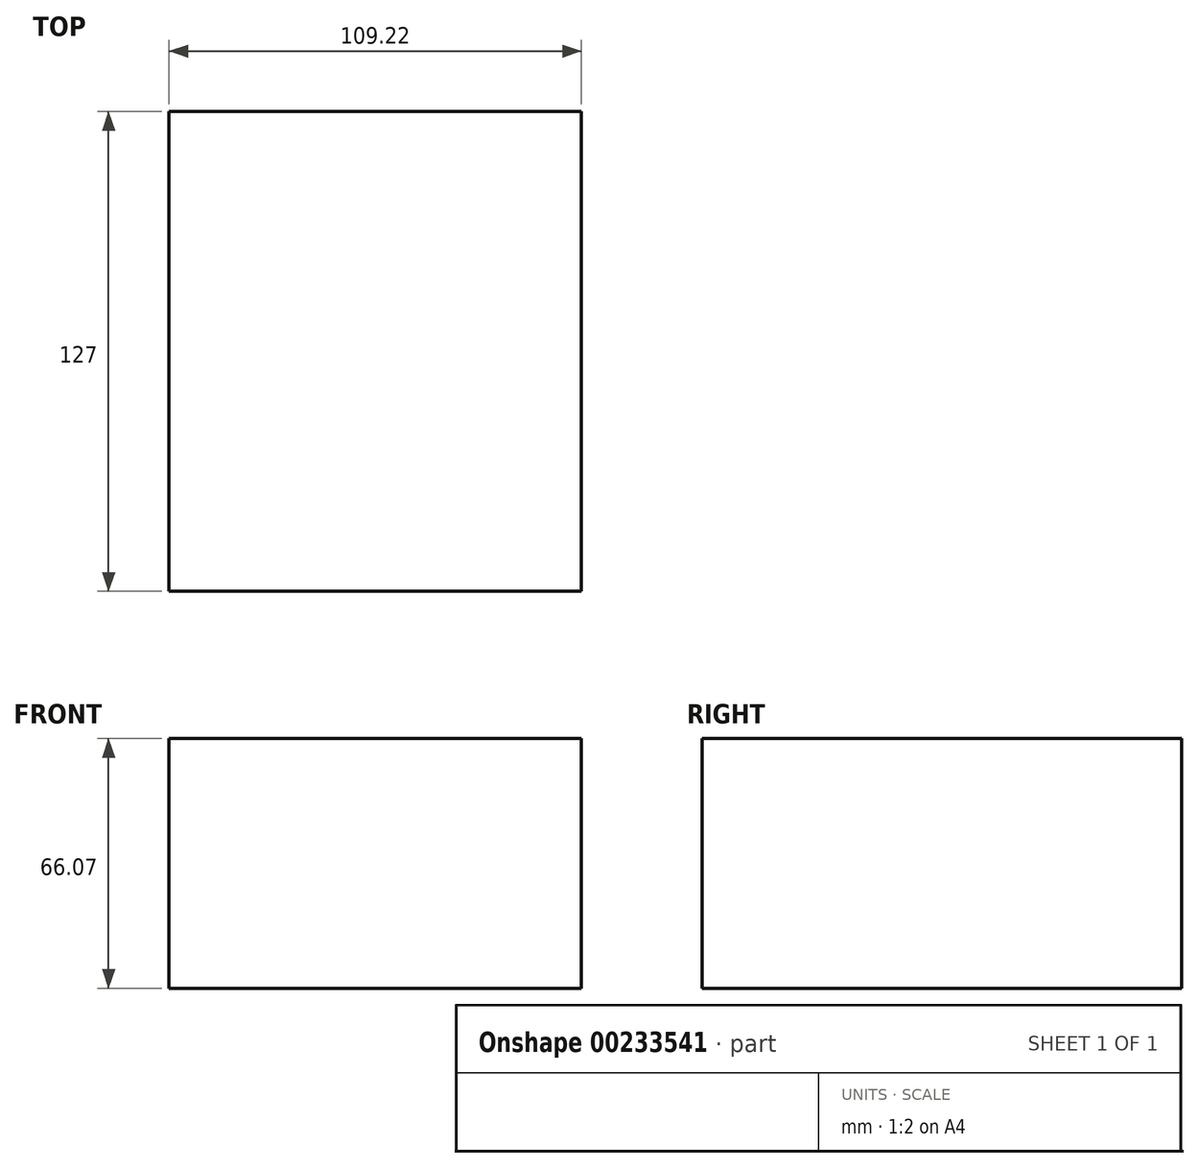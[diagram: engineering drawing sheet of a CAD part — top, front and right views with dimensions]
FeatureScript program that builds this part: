
annotation { "Feature Type Name" : "Feature", "Feature Type Description" : "" }
export const myFeature = defineFeature(function(context is Context, id is Id, definition is map)
    precondition{}
    {
        {
            var Q0;
            Q0=qCreatedBy(makeId("Front.planeOp"),FACE);
            var sketch = newSketch(context, id + "F0", { "sketchPlane" : qUnion([Q0])});
            skLineSegment(sketch, "E0.bottom", {"start": v(-34.9, 44.08) * mm, "end": v(74.33, 44.08) * mm});
            skLineSegment(sketch, "E0.top", {"start": v(-34.9, -21.99) * mm, "end": v(74.33, -21.99) * mm});
            skLineSegment(sketch, "E0.left", {"start": v(-34.9, 44.08) * mm, "end": v(-34.9, -21.99) * mm});
            skLineSegment(sketch, "E0.right", {"start": v(74.33, 44.08) * mm, "end": v(74.33, -21.99) * mm});
            skSolve(sketch);
        }
        {
            var Q0;
            Q0 = qSketchRegion(id + "F0", true);
            extrude(context, id + "F1", {"entities" : qUnion([Q0]), "depth" : 127 * mm});
        }
    });
